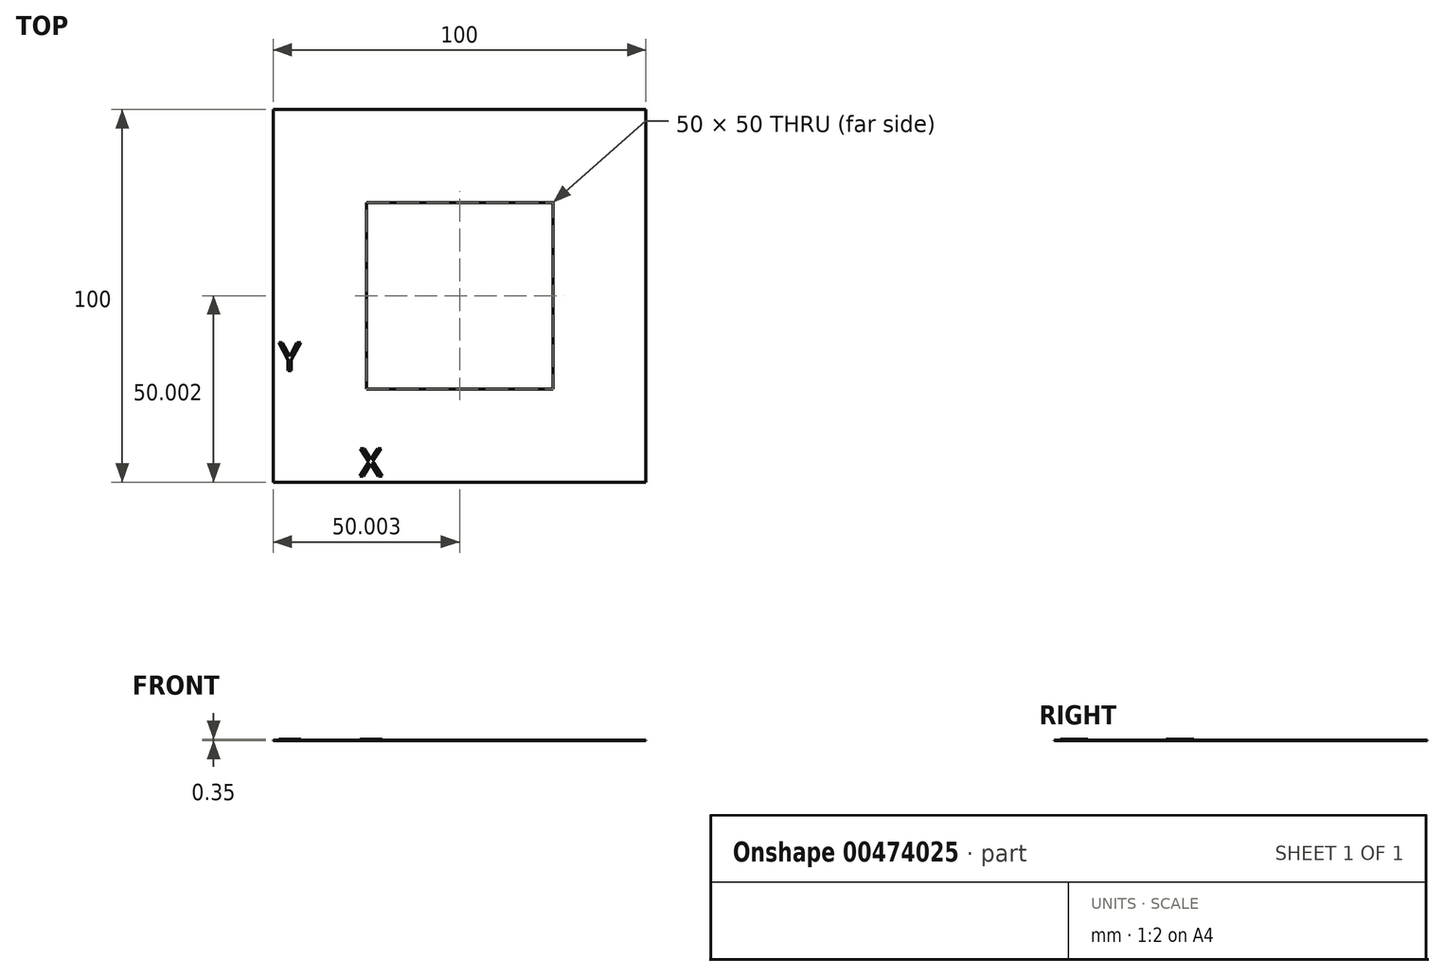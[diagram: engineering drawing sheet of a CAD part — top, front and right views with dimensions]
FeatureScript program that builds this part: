
annotation { "Feature Type Name" : "Feature", "Feature Type Description" : "" }
export const myFeature = defineFeature(function(context is Context, id is Id, definition is map)
    precondition{}
    {
        {
            var Q0;
            Q0=qCreatedBy(makeId("Top.planeOp"),FACE);
            var sketch = newSketch(context, id + "F0", { "sketchPlane" : qUnion([Q0])});
            skLineSegment(sketch, "E0.bottom", {"start": v(-35.72, 42.67) * mm, "end": v(64.28, 42.67) * mm});
            skLineSegment(sketch, "E0.top", {"start": v(-35.72, -57.33) * mm, "end": v(64.28, -57.33) * mm});
            skLineSegment(sketch, "E0.left", {"start": v(-35.72, 42.67) * mm, "end": v(-35.72, -57.33) * mm});
            skLineSegment(sketch, "E0.right", {"start": v(64.28, 42.67) * mm, "end": v(64.28, -57.33) * mm});
            skPoint(sketch, "E1", {"position": v(14.28, -7.33) * mm});
            skLineSegment(sketch, "E2.bottom", {"start": v(-10.72, 17.67) * mm, "end": v(39.28, 17.67) * mm});
            skLineSegment(sketch, "E2.top", {"start": v(-10.72, -32.33) * mm, "end": v(39.28, -32.33) * mm});
            skLineSegment(sketch, "E2.left", {"start": v(-10.72, 17.67) * mm, "end": v(-10.72, -32.33) * mm});
            skLineSegment(sketch, "E2.right", {"start": v(39.28, 17.67) * mm, "end": v(39.28, -32.33) * mm});
            skSolve(sketch);
        }
        {
            var Q0;
            Q0=qSketchRegion(id+"F0",true);
            extrude(context, id + "F1", {"entities" : qUnion([Q0]), "depth" : 0.09 * mm, "offsetDistance" : 25 * mm});
        }
        {
            var Q0;
            Q0=makeQuery(id+"F1.opExtrude","CAP_FACE",FACE,{"disambiguationData":[OSD([sQuery(id+"F0.wireOp",EDGE,"E0.bottom"),sQuery(id+"F0.wireOp",EDGE,"E0.top"),sQuery(id+"F0.wireOp",EDGE,"E0.left"),sQuery(id+"F0.wireOp",EDGE,"E0.right")])],"isStart":false});
            var sketch = newSketch(context, id + "F2", { "sketchPlane" : qUnion([Q0])});
            skPoint(sketch, "E3", {"position": v(14.28, -7.33) * mm});
            skText(sketch, "E4", { "text": "Y\n\n        X", "fontName": "OpenSans-Regular.ttf"});
            const initialGuessF2  = {"E4": [-0.03425, -0.02735, 1, 0, 0.00752]};
            skSetInitialGuess(sketch, initialGuessF2);
            skSolve(sketch);
        }
        {
            var Q0;
            Q0=qSketchRegion(id+"F2",true);
            extrude(context, id + "F3", {"entities" : qUnion([Q0]), "operationType" : NewBodyOperationType.ADD, "depth" : .2625 * mm, "offsetDistance" : 25 * mm});
        }
    });
